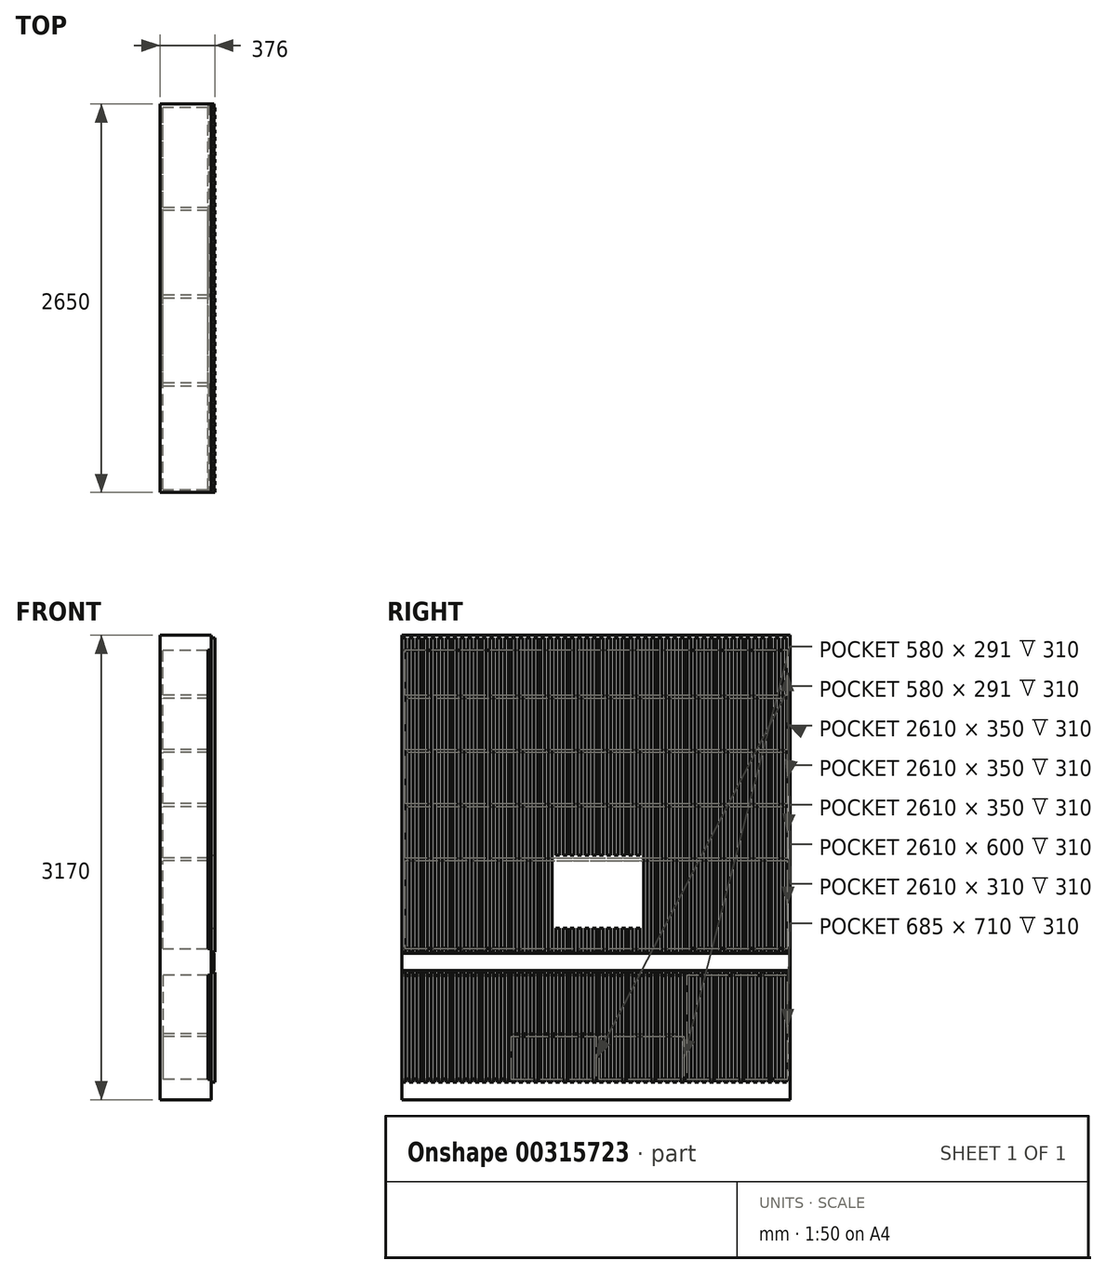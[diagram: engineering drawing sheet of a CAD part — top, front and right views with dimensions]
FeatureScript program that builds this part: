
annotation { "Feature Type Name" : "Feature", "Feature Type Description" : "" }
export const myFeature = defineFeature(function(context is Context, id is Id, definition is map)
    precondition{}
    {
        {
            var Q0;
            Q0=qCreatedBy(makeId("Top.planeOp"),FACE);
            var sketch = newSketch(context, id + "F0", { "sketchPlane" : qUnion([Q0])});
            skLineSegment(sketch, "E0.bottom", {"start": v(0, 0) * mm, "end": v(350, 0) * mm});
            skLineSegment(sketch, "E0.top", {"start": v(0, 2650) * mm, "end": v(350, 2650) * mm});
            skLineSegment(sketch, "E0.left", {"start": v(0, 0) * mm, "end": v(0, 2650) * mm});
            skLineSegment(sketch, "E0.right", {"start": v(350, 0) * mm, "end": v(350, 2650) * mm});
            skLineSegment(sketch, "E1", {"start": v(0, 2770) * mm, "end": v(350, 2770) * mm, "construction": true});
            skSolve(sketch);
        }
        {
            var Q0;
            Q0=qCreatedBy(makeId("Top.planeOp"),FACE);
            cPlane(context, id + "F1", {"entities" : qUnion([Q0]), "cplaneType" : CPlaneType.OFFSET, "offset" : 120 * mm, "width" : 150 * mm, "height" : 150 * mm});
        }
        {
            var Q0;
            Q0=makeQuery(id+"F0.imprint","IMPRINT",FACE,{"disambiguationData":[TD([[makeQuery(id+"F0.imprint","IMPRINT",EDGE,{"derivedFrom":sQuery(id+"F0.wireOp",EDGE,"E0.bottom")}),1.0]])]});
            extrude(context, id + "F2", {"entities" : qUnion([Q0]), "depth" : 3170 * mm});
        }
        {
            var Q0;
            Q0=makeQuery(id+"F2.opExtrude","SWEPT_FACE",FACE,{"disambiguationData":[OSD([sQuery(id+"F0.wireOp",EDGE,"E0.right")])]});
            var sketch = newSketch(context, id + "F3", { "sketchPlane" : qUnion([Q0])});
            skLineSegment(sketch, "E2.bottom", {"start": v(1035, 1670) * mm, "end": v(1635, 1670) * mm});
            skLineSegment(sketch, "E2.top", {"start": v(1035, 1170) * mm, "end": v(1635, 1170) * mm});
            skLineSegment(sketch, "E2.left", {"start": v(1035, 1670) * mm, "end": v(1035, 1170) * mm});
            skLineSegment(sketch, "E2.right", {"start": v(1635, 1670) * mm, "end": v(1635, 1170) * mm});
            skLineSegment(sketch, "E3", {"start": v(1035, 1670) * mm, "end": v(1635, 1170) * mm, "construction": true});
            skLineSegment(sketch, "E4", {"start": v(1635, 1670) * mm, "end": v(1035, 1170) * mm, "construction": true});
            skLineSegment(sketch, "E5", {"start": v(1335, 1420) * mm, "end": v(866.73, 1420) * mm, "construction": true});
            skPoint(sketch, "E5.endSnap0", {"position": v(1035, 1420) * mm});
            skLineSegment(sketch, "E6.bottom", {"start": v(1885, 1770) * mm, "end": v(785, 1770) * mm, "construction": true});
            skLineSegment(sketch, "E6.top", {"start": v(1885, 1070) * mm, "end": v(785, 1070) * mm, "construction": true});
            skLineSegment(sketch, "E6.left", {"start": v(1885, 1770) * mm, "end": v(1885, 1070) * mm, "construction": true});
            skLineSegment(sketch, "E6.right", {"start": v(785, 1770) * mm, "end": v(785, 1070) * mm, "construction": true});
            skPoint(sketch, "E6.middle", {"position": v(1335, 1420) * mm});
            skSolve(sketch);
        }
        {
            var Q0;
            Q0=qCreatedBy(makeId("Top.planeOp"),FACE);
            cPlane(context, id + "F4", {"entities" : qUnion([Q0]), "cplaneType" : CPlaneType.OFFSET, "offset" : 3150 * mm, "width" : 150 * mm, "height" : 150 * mm});
        }
        {
            var Q0;
            Q0=qCreatedBy(id+"F1.planeOp",FACE);
            var sketch = newSketch(context, id + "F5", { "sketchPlane" : qUnion([Q0])});
            skLineSegment(sketch, "E7.bottom", {"start": v(351, 0) * mm, "end": v(376, 0) * mm});
            skLineSegment(sketch, "E7.top", {"start": v(351, 25) * mm, "end": v(376, 25) * mm});
            skLineSegment(sketch, "E7.left", {"start": v(351, 0) * mm, "end": v(351, 25) * mm});
            skLineSegment(sketch, "E7.right", {"start": v(376, 0) * mm, "end": v(376, 25) * mm});
            skLineSegment(sketch, "E8.0.1.0", {"start": v(351, 75) * mm, "end": v(376, 75) * mm});
            skLineSegment(sketch, "E8.0.1.1", {"start": v(351, 50) * mm, "end": v(376, 50) * mm});
            skLineSegment(sketch, "E8.0.1.2", {"start": v(376, 50) * mm, "end": v(376, 75) * mm});
            skLineSegment(sketch, "E8.0.1.3", {"start": v(351, 50) * mm, "end": v(351, 75) * mm});
            skLineSegment(sketch, "E8.0.2.0", {"start": v(351, 125) * mm, "end": v(376, 125) * mm});
            skLineSegment(sketch, "E8.0.2.1", {"start": v(351, 100) * mm, "end": v(376, 100) * mm});
            skLineSegment(sketch, "E8.0.2.2", {"start": v(376, 100) * mm, "end": v(376, 125) * mm});
            skLineSegment(sketch, "E8.0.2.3", {"start": v(351, 100) * mm, "end": v(351, 125) * mm});
            skLineSegment(sketch, "E8.0.3.0", {"start": v(351, 175) * mm, "end": v(376, 175) * mm});
            skLineSegment(sketch, "E8.0.3.1", {"start": v(351, 150) * mm, "end": v(376, 150) * mm});
            skLineSegment(sketch, "E8.0.3.2", {"start": v(376, 150) * mm, "end": v(376, 175) * mm});
            skLineSegment(sketch, "E8.0.3.3", {"start": v(351, 150) * mm, "end": v(351, 175) * mm});
            skLineSegment(sketch, "E8.0.4.0", {"start": v(351, 225) * mm, "end": v(376, 225) * mm});
            skLineSegment(sketch, "E8.0.4.1", {"start": v(351, 200) * mm, "end": v(376, 200) * mm});
            skLineSegment(sketch, "E8.0.4.2", {"start": v(376, 200) * mm, "end": v(376, 225) * mm});
            skLineSegment(sketch, "E8.0.4.3", {"start": v(351, 200) * mm, "end": v(351, 225) * mm});
            skLineSegment(sketch, "E8.0.5.0", {"start": v(351, 275) * mm, "end": v(376, 275) * mm});
            skLineSegment(sketch, "E8.0.5.1", {"start": v(351, 250) * mm, "end": v(376, 250) * mm});
            skLineSegment(sketch, "E8.0.5.2", {"start": v(376, 250) * mm, "end": v(376, 275) * mm});
            skLineSegment(sketch, "E8.0.5.3", {"start": v(351, 250) * mm, "end": v(351, 275) * mm});
            skLineSegment(sketch, "E8.0.6.0", {"start": v(351, 325) * mm, "end": v(376, 325) * mm});
            skLineSegment(sketch, "E8.0.6.1", {"start": v(351, 300) * mm, "end": v(376, 300) * mm});
            skLineSegment(sketch, "E8.0.6.2", {"start": v(376, 300) * mm, "end": v(376, 325) * mm});
            skLineSegment(sketch, "E8.0.6.3", {"start": v(351, 300) * mm, "end": v(351, 325) * mm});
            skLineSegment(sketch, "E8.0.7.0", {"start": v(351, 375) * mm, "end": v(376, 375) * mm});
            skLineSegment(sketch, "E8.0.7.1", {"start": v(351, 350) * mm, "end": v(376, 350) * mm});
            skLineSegment(sketch, "E8.0.7.2", {"start": v(376, 350) * mm, "end": v(376, 375) * mm});
            skLineSegment(sketch, "E8.0.7.3", {"start": v(351, 350) * mm, "end": v(351, 375) * mm});
            skLineSegment(sketch, "E8.0.8.0", {"start": v(351, 425) * mm, "end": v(376, 425) * mm});
            skLineSegment(sketch, "E8.0.8.1", {"start": v(351, 400) * mm, "end": v(376, 400) * mm});
            skLineSegment(sketch, "E8.0.8.2", {"start": v(376, 400) * mm, "end": v(376, 425) * mm});
            skLineSegment(sketch, "E8.0.8.3", {"start": v(351, 400) * mm, "end": v(351, 425) * mm});
            skLineSegment(sketch, "E8.0.9.0", {"start": v(351, 475) * mm, "end": v(376, 475) * mm});
            skLineSegment(sketch, "E8.0.9.1", {"start": v(351, 450) * mm, "end": v(376, 450) * mm});
            skLineSegment(sketch, "E8.0.9.2", {"start": v(376, 450) * mm, "end": v(376, 475) * mm});
            skLineSegment(sketch, "E8.0.9.3", {"start": v(351, 450) * mm, "end": v(351, 475) * mm});
            skLineSegment(sketch, "E8.0.10.0", {"start": v(351, 525) * mm, "end": v(376, 525) * mm});
            skLineSegment(sketch, "E8.0.10.1", {"start": v(351, 500) * mm, "end": v(376, 500) * mm});
            skLineSegment(sketch, "E8.0.10.2", {"start": v(376, 500) * mm, "end": v(376, 525) * mm});
            skLineSegment(sketch, "E8.0.10.3", {"start": v(351, 500) * mm, "end": v(351, 525) * mm});
            skLineSegment(sketch, "E8.0.11.0", {"start": v(351, 575) * mm, "end": v(376, 575) * mm});
            skLineSegment(sketch, "E8.0.11.1", {"start": v(351, 550) * mm, "end": v(376, 550) * mm});
            skLineSegment(sketch, "E8.0.11.2", {"start": v(376, 550) * mm, "end": v(376, 575) * mm});
            skLineSegment(sketch, "E8.0.11.3", {"start": v(351, 550) * mm, "end": v(351, 575) * mm});
            skLineSegment(sketch, "E8.0.12.0", {"start": v(351, 625) * mm, "end": v(376, 625) * mm});
            skLineSegment(sketch, "E8.0.12.1", {"start": v(351, 600) * mm, "end": v(376, 600) * mm});
            skLineSegment(sketch, "E8.0.12.2", {"start": v(376, 600) * mm, "end": v(376, 625) * mm});
            skLineSegment(sketch, "E8.0.12.3", {"start": v(351, 600) * mm, "end": v(351, 625) * mm});
            skLineSegment(sketch, "E8.0.13.0", {"start": v(351, 675) * mm, "end": v(376, 675) * mm});
            skLineSegment(sketch, "E8.0.13.1", {"start": v(351, 650) * mm, "end": v(376, 650) * mm});
            skLineSegment(sketch, "E8.0.13.2", {"start": v(376, 650) * mm, "end": v(376, 675) * mm});
            skLineSegment(sketch, "E8.0.13.3", {"start": v(351, 650) * mm, "end": v(351, 675) * mm});
            skLineSegment(sketch, "E8.0.14.0", {"start": v(351, 725) * mm, "end": v(376, 725) * mm});
            skLineSegment(sketch, "E8.0.14.1", {"start": v(351, 700) * mm, "end": v(376, 700) * mm});
            skLineSegment(sketch, "E8.0.14.2", {"start": v(376, 700) * mm, "end": v(376, 725) * mm});
            skLineSegment(sketch, "E8.0.14.3", {"start": v(351, 700) * mm, "end": v(351, 725) * mm});
            skLineSegment(sketch, "E8.0.15.0", {"start": v(351, 775) * mm, "end": v(376, 775) * mm});
            skLineSegment(sketch, "E8.0.15.1", {"start": v(351, 750) * mm, "end": v(376, 750) * mm});
            skLineSegment(sketch, "E8.0.15.2", {"start": v(376, 750) * mm, "end": v(376, 775) * mm});
            skLineSegment(sketch, "E8.0.15.3", {"start": v(351, 750) * mm, "end": v(351, 775) * mm});
            skLineSegment(sketch, "E8.0.16.0", {"start": v(351, 825) * mm, "end": v(376, 825) * mm});
            skLineSegment(sketch, "E8.0.16.1", {"start": v(351, 800) * mm, "end": v(376, 800) * mm});
            skLineSegment(sketch, "E8.0.16.2", {"start": v(376, 800) * mm, "end": v(376, 825) * mm});
            skLineSegment(sketch, "E8.0.16.3", {"start": v(351, 800) * mm, "end": v(351, 825) * mm});
            skLineSegment(sketch, "E8.0.17.0", {"start": v(351, 875) * mm, "end": v(376, 875) * mm});
            skLineSegment(sketch, "E8.0.17.1", {"start": v(351, 850) * mm, "end": v(376, 850) * mm});
            skLineSegment(sketch, "E8.0.17.2", {"start": v(376, 850) * mm, "end": v(376, 875) * mm});
            skLineSegment(sketch, "E8.0.17.3", {"start": v(351, 850) * mm, "end": v(351, 875) * mm});
            skLineSegment(sketch, "E8.0.18.0", {"start": v(351, 925) * mm, "end": v(376, 925) * mm});
            skLineSegment(sketch, "E8.0.18.1", {"start": v(351, 900) * mm, "end": v(376, 900) * mm});
            skLineSegment(sketch, "E8.0.18.2", {"start": v(376, 900) * mm, "end": v(376, 925) * mm});
            skLineSegment(sketch, "E8.0.18.3", {"start": v(351, 900) * mm, "end": v(351, 925) * mm});
            skLineSegment(sketch, "E8.0.19.0", {"start": v(351, 975) * mm, "end": v(376, 975) * mm});
            skLineSegment(sketch, "E8.0.19.1", {"start": v(351, 950) * mm, "end": v(376, 950) * mm});
            skLineSegment(sketch, "E8.0.19.2", {"start": v(376, 950) * mm, "end": v(376, 975) * mm});
            skLineSegment(sketch, "E8.0.19.3", {"start": v(351, 950) * mm, "end": v(351, 975) * mm});
            skLineSegment(sketch, "E8.0.20.0", {"start": v(351, 1025) * mm, "end": v(376, 1025) * mm});
            skLineSegment(sketch, "E8.0.20.1", {"start": v(351, 1000) * mm, "end": v(376, 1000) * mm});
            skLineSegment(sketch, "E8.0.20.2", {"start": v(376, 1000) * mm, "end": v(376, 1025) * mm});
            skLineSegment(sketch, "E8.0.20.3", {"start": v(351, 1000) * mm, "end": v(351, 1025) * mm});
            skLineSegment(sketch, "E8.0.21.0", {"start": v(351, 1075) * mm, "end": v(376, 1075) * mm});
            skLineSegment(sketch, "E8.0.21.1", {"start": v(351, 1050) * mm, "end": v(376, 1050) * mm});
            skLineSegment(sketch, "E8.0.21.2", {"start": v(376, 1050) * mm, "end": v(376, 1075) * mm});
            skLineSegment(sketch, "E8.0.21.3", {"start": v(351, 1050) * mm, "end": v(351, 1075) * mm});
            skLineSegment(sketch, "E8.direction1", {"start": v(351, 0) * mm, "end": v(376, 0) * mm, "construction": true});
            skLineSegment(sketch, "E8.direction2", {"start": v(351, 0) * mm, "end": v(351, 50) * mm, "construction": true});
            skLineSegment(sketch, "E9.0.0.22", {"start": v(351, 1125) * mm, "end": v(376, 1125) * mm});
            skLineSegment(sketch, "E9.3.0.22", {"start": v(351, 1100) * mm, "end": v(376, 1100) * mm});
            skLineSegment(sketch, "E9.6.0.22", {"start": v(376, 1100) * mm, "end": v(376, 1125) * mm});
            skLineSegment(sketch, "E9.9.0.22", {"start": v(351, 1100) * mm, "end": v(351, 1125) * mm});
            skLineSegment(sketch, "E9.0.0.23", {"start": v(351, 1175) * mm, "end": v(376, 1175) * mm});
            skLineSegment(sketch, "E9.3.0.23", {"start": v(351, 1150) * mm, "end": v(376, 1150) * mm});
            skLineSegment(sketch, "E9.6.0.23", {"start": v(376, 1150) * mm, "end": v(376, 1175) * mm});
            skLineSegment(sketch, "E9.9.0.23", {"start": v(351, 1150) * mm, "end": v(351, 1175) * mm});
            skLineSegment(sketch, "E9.0.0.24", {"start": v(351, 1225) * mm, "end": v(376, 1225) * mm});
            skLineSegment(sketch, "E9.3.0.24", {"start": v(351, 1200) * mm, "end": v(376, 1200) * mm});
            skLineSegment(sketch, "E9.6.0.24", {"start": v(376, 1200) * mm, "end": v(376, 1225) * mm});
            skLineSegment(sketch, "E9.9.0.24", {"start": v(351, 1200) * mm, "end": v(351, 1225) * mm});
            skLineSegment(sketch, "E10.0.0.25", {"start": v(351, 1275) * mm, "end": v(376, 1275) * mm});
            skLineSegment(sketch, "E10.3.0.25", {"start": v(351, 1250) * mm, "end": v(376, 1250) * mm});
            skLineSegment(sketch, "E10.6.0.25", {"start": v(376, 1250) * mm, "end": v(376, 1275) * mm});
            skLineSegment(sketch, "E10.9.0.25", {"start": v(351, 1250) * mm, "end": v(351, 1275) * mm});
            skLineSegment(sketch, "E10.0.0.26", {"start": v(351, 1325) * mm, "end": v(376, 1325) * mm});
            skLineSegment(sketch, "E10.3.0.26", {"start": v(351, 1300) * mm, "end": v(376, 1300) * mm});
            skLineSegment(sketch, "E10.6.0.26", {"start": v(376, 1300) * mm, "end": v(376, 1325) * mm});
            skLineSegment(sketch, "E10.9.0.26", {"start": v(351, 1300) * mm, "end": v(351, 1325) * mm});
            skLineSegment(sketch, "E10.0.0.27", {"start": v(351, 1375) * mm, "end": v(376, 1375) * mm});
            skLineSegment(sketch, "E10.3.0.27", {"start": v(351, 1350) * mm, "end": v(376, 1350) * mm});
            skLineSegment(sketch, "E10.6.0.27", {"start": v(376, 1350) * mm, "end": v(376, 1375) * mm});
            skLineSegment(sketch, "E10.9.0.27", {"start": v(351, 1350) * mm, "end": v(351, 1375) * mm});
            skLineSegment(sketch, "E10.0.0.28", {"start": v(351, 1425) * mm, "end": v(376, 1425) * mm});
            skLineSegment(sketch, "E10.3.0.28", {"start": v(351, 1400) * mm, "end": v(376, 1400) * mm});
            skLineSegment(sketch, "E10.6.0.28", {"start": v(376, 1400) * mm, "end": v(376, 1425) * mm});
            skLineSegment(sketch, "E10.9.0.28", {"start": v(351, 1400) * mm, "end": v(351, 1425) * mm});
            skLineSegment(sketch, "E10.0.0.29", {"start": v(351, 1475) * mm, "end": v(376, 1475) * mm});
            skLineSegment(sketch, "E10.3.0.29", {"start": v(351, 1450) * mm, "end": v(376, 1450) * mm});
            skLineSegment(sketch, "E10.6.0.29", {"start": v(376, 1450) * mm, "end": v(376, 1475) * mm});
            skLineSegment(sketch, "E10.9.0.29", {"start": v(351, 1450) * mm, "end": v(351, 1475) * mm});
            skLineSegment(sketch, "E10.0.0.30", {"start": v(351, 1525) * mm, "end": v(376, 1525) * mm});
            skLineSegment(sketch, "E10.3.0.30", {"start": v(351, 1500) * mm, "end": v(376, 1500) * mm});
            skLineSegment(sketch, "E10.6.0.30", {"start": v(376, 1500) * mm, "end": v(376, 1525) * mm});
            skLineSegment(sketch, "E10.9.0.30", {"start": v(351, 1500) * mm, "end": v(351, 1525) * mm});
            skLineSegment(sketch, "E10.0.0.31", {"start": v(351, 1575) * mm, "end": v(376, 1575) * mm});
            skLineSegment(sketch, "E10.3.0.31", {"start": v(351, 1550) * mm, "end": v(376, 1550) * mm});
            skLineSegment(sketch, "E10.6.0.31", {"start": v(376, 1550) * mm, "end": v(376, 1575) * mm});
            skLineSegment(sketch, "E10.9.0.31", {"start": v(351, 1550) * mm, "end": v(351, 1575) * mm});
            skLineSegment(sketch, "E10.0.0.32", {"start": v(351, 1625) * mm, "end": v(376, 1625) * mm});
            skLineSegment(sketch, "E10.3.0.32", {"start": v(351, 1600) * mm, "end": v(376, 1600) * mm});
            skLineSegment(sketch, "E10.6.0.32", {"start": v(376, 1600) * mm, "end": v(376, 1625) * mm});
            skLineSegment(sketch, "E10.9.0.32", {"start": v(351, 1600) * mm, "end": v(351, 1625) * mm});
            skLineSegment(sketch, "E10.0.0.33", {"start": v(351, 1675) * mm, "end": v(376, 1675) * mm});
            skLineSegment(sketch, "E10.3.0.33", {"start": v(351, 1650) * mm, "end": v(376, 1650) * mm});
            skLineSegment(sketch, "E10.6.0.33", {"start": v(376, 1650) * mm, "end": v(376, 1675) * mm});
            skLineSegment(sketch, "E10.9.0.33", {"start": v(351, 1650) * mm, "end": v(351, 1675) * mm});
            skLineSegment(sketch, "E10.0.0.34", {"start": v(351, 1725) * mm, "end": v(376, 1725) * mm});
            skLineSegment(sketch, "E10.3.0.34", {"start": v(351, 1700) * mm, "end": v(376, 1700) * mm});
            skLineSegment(sketch, "E10.6.0.34", {"start": v(376, 1700) * mm, "end": v(376, 1725) * mm});
            skLineSegment(sketch, "E10.9.0.34", {"start": v(351, 1700) * mm, "end": v(351, 1725) * mm});
            skLineSegment(sketch, "E10.0.0.35", {"start": v(351, 1775) * mm, "end": v(376, 1775) * mm});
            skLineSegment(sketch, "E10.3.0.35", {"start": v(351, 1750) * mm, "end": v(376, 1750) * mm});
            skLineSegment(sketch, "E10.6.0.35", {"start": v(376, 1750) * mm, "end": v(376, 1775) * mm});
            skLineSegment(sketch, "E10.9.0.35", {"start": v(351, 1750) * mm, "end": v(351, 1775) * mm});
            skLineSegment(sketch, "E10.0.0.36", {"start": v(351, 1825) * mm, "end": v(376, 1825) * mm});
            skLineSegment(sketch, "E10.3.0.36", {"start": v(351, 1800) * mm, "end": v(376, 1800) * mm});
            skLineSegment(sketch, "E10.6.0.36", {"start": v(376, 1800) * mm, "end": v(376, 1825) * mm});
            skLineSegment(sketch, "E10.9.0.36", {"start": v(351, 1800) * mm, "end": v(351, 1825) * mm});
            skLineSegment(sketch, "E10.0.0.37", {"start": v(351, 1875) * mm, "end": v(376, 1875) * mm});
            skLineSegment(sketch, "E10.3.0.37", {"start": v(351, 1850) * mm, "end": v(376, 1850) * mm});
            skLineSegment(sketch, "E10.6.0.37", {"start": v(376, 1850) * mm, "end": v(376, 1875) * mm});
            skLineSegment(sketch, "E10.9.0.37", {"start": v(351, 1850) * mm, "end": v(351, 1875) * mm});
            skLineSegment(sketch, "E10.0.0.38", {"start": v(351, 1925) * mm, "end": v(376, 1925) * mm});
            skLineSegment(sketch, "E10.3.0.38", {"start": v(351, 1900) * mm, "end": v(376, 1900) * mm});
            skLineSegment(sketch, "E10.6.0.38", {"start": v(376, 1900) * mm, "end": v(376, 1925) * mm});
            skLineSegment(sketch, "E10.9.0.38", {"start": v(351, 1900) * mm, "end": v(351, 1925) * mm});
            skLineSegment(sketch, "E10.0.0.39", {"start": v(351, 1975) * mm, "end": v(376, 1975) * mm});
            skLineSegment(sketch, "E10.3.0.39", {"start": v(351, 1950) * mm, "end": v(376, 1950) * mm});
            skLineSegment(sketch, "E10.6.0.39", {"start": v(376, 1950) * mm, "end": v(376, 1975) * mm});
            skLineSegment(sketch, "E10.9.0.39", {"start": v(351, 1950) * mm, "end": v(351, 1975) * mm});
            skLineSegment(sketch, "E10.0.0.40", {"start": v(351, 2025) * mm, "end": v(376, 2025) * mm});
            skLineSegment(sketch, "E10.3.0.40", {"start": v(351, 2000) * mm, "end": v(376, 2000) * mm});
            skLineSegment(sketch, "E10.6.0.40", {"start": v(376, 2000) * mm, "end": v(376, 2025) * mm});
            skLineSegment(sketch, "E10.9.0.40", {"start": v(351, 2000) * mm, "end": v(351, 2025) * mm});
            skLineSegment(sketch, "E10.0.0.41", {"start": v(351, 2075) * mm, "end": v(376, 2075) * mm});
            skLineSegment(sketch, "E10.3.0.41", {"start": v(351, 2050) * mm, "end": v(376, 2050) * mm});
            skLineSegment(sketch, "E10.6.0.41", {"start": v(376, 2050) * mm, "end": v(376, 2075) * mm});
            skLineSegment(sketch, "E10.9.0.41", {"start": v(351, 2050) * mm, "end": v(351, 2075) * mm});
            skLineSegment(sketch, "E10.0.0.42", {"start": v(351, 2125) * mm, "end": v(376, 2125) * mm});
            skLineSegment(sketch, "E10.3.0.42", {"start": v(351, 2100) * mm, "end": v(376, 2100) * mm});
            skLineSegment(sketch, "E10.6.0.42", {"start": v(376, 2100) * mm, "end": v(376, 2125) * mm});
            skLineSegment(sketch, "E10.9.0.42", {"start": v(351, 2100) * mm, "end": v(351, 2125) * mm});
            skLineSegment(sketch, "E10.0.0.43", {"start": v(351, 2175) * mm, "end": v(376, 2175) * mm});
            skLineSegment(sketch, "E10.3.0.43", {"start": v(351, 2150) * mm, "end": v(376, 2150) * mm});
            skLineSegment(sketch, "E10.6.0.43", {"start": v(376, 2150) * mm, "end": v(376, 2175) * mm});
            skLineSegment(sketch, "E10.9.0.43", {"start": v(351, 2150) * mm, "end": v(351, 2175) * mm});
            skLineSegment(sketch, "E10.0.0.44", {"start": v(351, 2225) * mm, "end": v(376, 2225) * mm});
            skLineSegment(sketch, "E10.3.0.44", {"start": v(351, 2200) * mm, "end": v(376, 2200) * mm});
            skLineSegment(sketch, "E10.6.0.44", {"start": v(376, 2200) * mm, "end": v(376, 2225) * mm});
            skLineSegment(sketch, "E10.9.0.44", {"start": v(351, 2200) * mm, "end": v(351, 2225) * mm});
            skLineSegment(sketch, "E10.0.0.45", {"start": v(351, 2275) * mm, "end": v(376, 2275) * mm});
            skLineSegment(sketch, "E10.3.0.45", {"start": v(351, 2250) * mm, "end": v(376, 2250) * mm});
            skLineSegment(sketch, "E10.6.0.45", {"start": v(376, 2250) * mm, "end": v(376, 2275) * mm});
            skLineSegment(sketch, "E10.9.0.45", {"start": v(351, 2250) * mm, "end": v(351, 2275) * mm});
            skLineSegment(sketch, "E10.0.0.46", {"start": v(351, 2325) * mm, "end": v(376, 2325) * mm});
            skLineSegment(sketch, "E10.3.0.46", {"start": v(351, 2300) * mm, "end": v(376, 2300) * mm});
            skLineSegment(sketch, "E10.6.0.46", {"start": v(376, 2300) * mm, "end": v(376, 2325) * mm});
            skLineSegment(sketch, "E10.9.0.46", {"start": v(351, 2300) * mm, "end": v(351, 2325) * mm});
            skLineSegment(sketch, "E10.0.0.47", {"start": v(351, 2375) * mm, "end": v(376, 2375) * mm});
            skLineSegment(sketch, "E10.3.0.47", {"start": v(351, 2350) * mm, "end": v(376, 2350) * mm});
            skLineSegment(sketch, "E10.6.0.47", {"start": v(376, 2350) * mm, "end": v(376, 2375) * mm});
            skLineSegment(sketch, "E10.9.0.47", {"start": v(351, 2350) * mm, "end": v(351, 2375) * mm});
            skLineSegment(sketch, "E10.0.0.48", {"start": v(351, 2425) * mm, "end": v(376, 2425) * mm});
            skLineSegment(sketch, "E10.3.0.48", {"start": v(351, 2400) * mm, "end": v(376, 2400) * mm});
            skLineSegment(sketch, "E10.6.0.48", {"start": v(376, 2400) * mm, "end": v(376, 2425) * mm});
            skLineSegment(sketch, "E10.9.0.48", {"start": v(351, 2400) * mm, "end": v(351, 2425) * mm});
            skLineSegment(sketch, "E10.0.0.49", {"start": v(351, 2475) * mm, "end": v(376, 2475) * mm});
            skLineSegment(sketch, "E10.3.0.49", {"start": v(351, 2450) * mm, "end": v(376, 2450) * mm});
            skLineSegment(sketch, "E10.6.0.49", {"start": v(376, 2450) * mm, "end": v(376, 2475) * mm});
            skLineSegment(sketch, "E10.9.0.49", {"start": v(351, 2450) * mm, "end": v(351, 2475) * mm});
            skLineSegment(sketch, "E11.0.0.50", {"start": v(351, 2525) * mm, "end": v(376, 2525) * mm});
            skLineSegment(sketch, "E11.3.0.50", {"start": v(351, 2500) * mm, "end": v(376, 2500) * mm});
            skLineSegment(sketch, "E11.6.0.50", {"start": v(376, 2500) * mm, "end": v(376, 2525) * mm});
            skLineSegment(sketch, "E11.9.0.50", {"start": v(351, 2500) * mm, "end": v(351, 2525) * mm});
            skLineSegment(sketch, "E11.0.0.51", {"start": v(351, 2575) * mm, "end": v(376, 2575) * mm});
            skLineSegment(sketch, "E11.3.0.51", {"start": v(351, 2550) * mm, "end": v(376, 2550) * mm});
            skLineSegment(sketch, "E11.6.0.51", {"start": v(376, 2550) * mm, "end": v(376, 2575) * mm});
            skLineSegment(sketch, "E11.9.0.51", {"start": v(351, 2550) * mm, "end": v(351, 2575) * mm});
            skLineSegment(sketch, "E11.0.0.52", {"start": v(351, 2625) * mm, "end": v(376, 2625) * mm});
            skLineSegment(sketch, "E11.3.0.52", {"start": v(351, 2600) * mm, "end": v(376, 2600) * mm});
            skLineSegment(sketch, "E11.6.0.52", {"start": v(376, 2600) * mm, "end": v(376, 2625) * mm});
            skLineSegment(sketch, "E11.9.0.52", {"start": v(351, 2600) * mm, "end": v(351, 2625) * mm});
            skSolve(sketch);
        }
        {
            var Q0;
            Q0=qSketchRegion(id+"F5",true);
            var Q1;
            Q1=qCreatedBy(id+"F4.planeOp",FACE);
            extrude(context, id + "F6", {"entities" : qUnion([Q0]), "endBound" : BoundingType.UP_TO_SURFACE, "endBoundEntityFace" : qUnion([Q1]), "depth" : 2525 * mm});
        }
        {
            var Q0;
            Q0 = qSketchRegion(id + "F3", true);
            extrude(context, id + "F7", {"entities" : qUnion([Q0]), "operationType" : NewBodyOperationType.REMOVE, "endBound" : BoundingType.THROUGH_ALL, "depth" : 25 * mm});
        }
        {
            var Q0;
            Q0=makeQuery(id+"F2.opExtrude","SWEPT_FACE",FACE,{"disambiguationData":[OSD([sQuery(id+"F0.wireOp",EDGE,"E0.left")])]});
            cPlane(context, id + "F8", {"entities" : qUnion([Q0]), "cplaneType" : CPlaneType.OFFSET, "offset" : 20 * mm, "oppositeDirection" : true, "width" : 150 * mm, "height" : 150 * mm});
        }
        {
            var Q0;
            Q0=makeQuery(id+"F2.opExtrude","SWEPT_FACE",FACE,{"disambiguationData":[OSD([sQuery(id+"F0.wireOp",EDGE,"E0.right")])]});
            var sketch = newSketch(context, id + "F9", { "sketchPlane" : qUnion([Q0])});
            skLineSegment(sketch, "E12.bottom", {"start": v(-252.85, 1010) * mm, "end": v(2905.96, 1010) * mm});
            skLineSegment(sketch, "E12.top", {"start": v(-252.85, 870) * mm, "end": v(2905.96, 870) * mm});
            skLineSegment(sketch, "E12.left", {"start": v(-252.85, 1010) * mm, "end": v(-252.85, 870) * mm});
            skLineSegment(sketch, "E12.right", {"start": v(2905.96, 1010) * mm, "end": v(2905.96, 870) * mm});
            skSolve(sketch);
        }
        {
            var Q0;
            Q0 = qSketchRegion(id + "F9", true);
            extrude(context, id + "F10", {"entities" : qUnion([Q0]), "operationType" : NewBodyOperationType.REMOVE, "endBound" : BoundingType.THROUGH_ALL, "depth" : 25 * mm});
        }
        {
            var Q0;
            {var subQ1=sQuery(id+"F0.wireOp",EDGE,"E0.right");var subQ6=makeQuery(id+"F2.opExtrude","CAP_EDGE",EDGE,{"disambiguationData":[OSD([subQ1])],"isStart":true});Q0=makeQuery(id+"F9.imprint","IMPRINT",FACE,{"disambiguationData":[TD([[makeQuery(id+"F9.imprint","IMPRINT",EDGE,{"derivedFrom":subQ6}),1.0]])]});}
            cPlane(context, id + "F11", {"entities" : qUnion([Q0]), "cplaneType" : CPlaneType.OFFSET, "offset" : 20 * mm, "oppositeDirection" : true, "width" : 150 * mm, "height" : 150 * mm});
        }
        {
            var Q0;
            Q0=makeQuery(id+"F3.imprint","IMPRINT",FACE,{"disambiguationData":[TD([[makeQuery(id+"F3.imprint","IMPRINT",EDGE,{"derivedFrom":sQuery(id+"F3.wireOp",EDGE,"E2.bottom")}),1.0]])]});
            var sketch = newSketch(context, id + "F12", { "sketchPlane" : qUnion([Q0])});
            skLineSegment(sketch, "E13.bottom", {"start": v(0, 1000) * mm, "end": v(2650, 1000) * mm});
            skLineSegment(sketch, "E13.top", {"start": v(0, 880) * mm, "end": v(2650, 880) * mm});
            skLineSegment(sketch, "E13.left", {"start": v(0, 1000) * mm, "end": v(0, 880) * mm});
            skLineSegment(sketch, "E13.right", {"start": v(2650, 1000) * mm, "end": v(2650, 880) * mm});
            skSolve(sketch);
        }
        {
            var Q0;
            Q0 = qSketchRegion(id + "F12", true);
            extrude(context, id + "F13", {"entities" : qUnion([Q0]), "depth" : 20 * mm});
        }
        {
            var Q0;
            Q0=makeQuery(id+"F3.imprint","IMPRINT",FACE,{"disambiguationData":[TD([[makeQuery(id+"F3.imprint","IMPRINT",EDGE,{"derivedFrom":sQuery(id+"F3.wireOp",EDGE,"E2.bottom")}),1.0]])]});
            var sketch = newSketch(context, id + "F14", { "sketchPlane" : qUnion([Q0])});
            skLineSegment(sketch, "E14.bottom", {"start": v(0, 850) * mm, "end": v(2650, 850) * mm});
            skLineSegment(sketch, "E14.top", {"start": v(0, 140) * mm, "end": v(2650, 140) * mm});
            skLineSegment(sketch, "E14.left", {"start": v(0, 850) * mm, "end": v(0, 140) * mm});
            skLineSegment(sketch, "E14.right", {"start": v(2650, 850) * mm, "end": v(2650, 140) * mm});
            skLineSegment(sketch, "E15.bottom", {"start": v(0, 3070) * mm, "end": v(2650, 3070) * mm});
            skLineSegment(sketch, "E15.top", {"start": v(0, 1030) * mm, "end": v(2650, 1030) * mm});
            skLineSegment(sketch, "E15.left", {"start": v(0, 3070) * mm, "end": v(0, 1030) * mm});
            skLineSegment(sketch, "E15.right", {"start": v(2650, 3070) * mm, "end": v(2650, 1030) * mm});
            skSolve(sketch);
        }
        {
            var Q0;
            Q0 = qSketchRegion(id + "F14", true);
            var Q1;
            Q1=qCreatedBy(id+"F11.planeOp",FACE);
            extrude(context, id + "F15", {"entities" : qUnion([Q0]), "operationType" : NewBodyOperationType.REMOVE, "endBound" : BoundingType.UP_TO_SURFACE, "oppositeDirection" : true, "endBoundEntityFace" : qUnion([Q1]), "depth" : 20 * mm});
        }
        {
            var Q0;
            Q0=qCreatedBy(id+"F11.planeOp",FACE);
            var sketch = newSketch(context, id + "F16", { "sketchPlane" : qUnion([Q0])});
            skLineSegment(sketch, "E16.bottom", {"start": v(20, 850) * mm, "end": v(2630, 850) * mm});
            skLineSegment(sketch, "E16.top", {"start": v(20, 140) * mm, "end": v(2630, 140) * mm});
            skLineSegment(sketch, "E16.left", {"start": v(20, 850) * mm, "end": v(20, 140) * mm});
            skLineSegment(sketch, "E16.right", {"start": v(2630, 850) * mm, "end": v(2630, 140) * mm});
            skLineSegment(sketch, "E17.bottom", {"start": v(20, 1030) * mm, "end": v(2630, 1030) * mm});
            skLineSegment(sketch, "E17.top", {"start": v(20, 3070) * mm, "end": v(2630, 3070) * mm});
            skLineSegment(sketch, "E17.left", {"start": v(20, 1030) * mm, "end": v(20, 3070) * mm});
            skLineSegment(sketch, "E17.right", {"start": v(2630, 1030) * mm, "end": v(2630, 3070) * mm});
            skSolve(sketch);
        }
        {
            var Q0;
            Q0 = qSketchRegion(id + "F16", true);
            var Q1;
            Q1=qCreatedBy(id+"F8.planeOp",FACE);
            extrude(context, id + "F17", {"entities" : qUnion([Q0]), "operationType" : NewBodyOperationType.REMOVE, "endBound" : BoundingType.UP_TO_SURFACE, "oppositeDirection" : true, "endBoundEntityFace" : qUnion([Q1]), "depth" : 25 * mm});
        }
        {
            var Q0;
            Q0=qCreatedBy(id+"F8.planeOp",FACE);
            var sketch = newSketch(context, id + "F18", { "sketchPlane" : qUnion([Q0])});
            skLineSegment(sketch, "E18.bottom", {"start": v(-725, 3070) * mm, "end": v(-745, 3070) * mm});
            skLineSegment(sketch, "E18.left", {"start": v(-725, 3070) * mm, "end": v(-725, 1850) * mm});
            skLineSegment(sketch, "E18.right", {"start": v(-745, 3070) * mm, "end": v(-745, 1850) * mm});
            skLineSegment(sketch, "E19.bottom", {"start": v(-1925, 3070) * mm, "end": v(-1945, 3070) * mm});
            skLineSegment(sketch, "E19.left", {"start": v(-1925, 3070) * mm, "end": v(-1925, 1850) * mm});
            skLineSegment(sketch, "E19.right", {"start": v(-1945, 3070) * mm, "end": v(-1945, 1850) * mm});
            skLineSegment(sketch, "E20.bottom", {"start": v(-1945, 850) * mm, "end": v(-1925, 850) * mm});
            skLineSegment(sketch, "E20.top", {"start": v(-1945, 140) * mm, "end": v(-1925, 140) * mm});
            skLineSegment(sketch, "E20.left", {"start": v(-1945, 850) * mm, "end": v(-1945, 140) * mm});
            skLineSegment(sketch, "E20.right", {"start": v(-1925, 850) * mm, "end": v(-1925, 140) * mm});
            skLineSegment(sketch, "E21.bottom", {"start": v(-745, 850) * mm, "end": v(-725, 850) * mm});
            skLineSegment(sketch, "E21.top", {"start": v(-745, 140) * mm, "end": v(-725, 140) * mm});
            skLineSegment(sketch, "E21.left", {"start": v(-745, 850) * mm, "end": v(-745, 140) * mm});
            skLineSegment(sketch, "E21.right", {"start": v(-725, 850) * mm, "end": v(-725, 140) * mm});
            skLineSegment(sketch, "E22.bottom", {"start": v(-1325, 850) * mm, "end": v(-1345, 850) * mm});
            skLineSegment(sketch, "E22.top", {"start": v(-1325, 140) * mm, "end": v(-1345, 140) * mm});
            skLineSegment(sketch, "E22.left", {"start": v(-1325, 850) * mm, "end": v(-1325, 140) * mm});
            skLineSegment(sketch, "E22.right", {"start": v(-1345, 850) * mm, "end": v(-1345, 140) * mm});
            skLineSegment(sketch, "E23.bottom", {"start": v(-20, 1850) * mm, "end": v(-2630, 1850) * mm});
            skLineSegment(sketch, "E23.top", {"start": v(-20, 1830) * mm, "end": v(-2630, 1830) * mm});
            skLineSegment(sketch, "E23.left", {"start": v(-20, 1850) * mm, "end": v(-20, 1830) * mm});
            skLineSegment(sketch, "E23.right", {"start": v(-2630, 1850) * mm, "end": v(-2630, 1830) * mm});
            skLineSegment(sketch, "E24.bottom", {"start": v(-1325, 1850) * mm, "end": v(-1345, 1850) * mm});
            skLineSegment(sketch, "E24.top", {"start": v(-1325, 3070) * mm, "end": v(-1345, 3070) * mm});
            skLineSegment(sketch, "E24.left", {"start": v(-1325, 1850) * mm, "end": v(-1325, 3070) * mm});
            skLineSegment(sketch, "E24.right", {"start": v(-1345, 1850) * mm, "end": v(-1345, 3070) * mm});
            skSolve(sketch);
        }
        {
            var Q0;
            Q0=qCreatedBy(id+"F8.planeOp",FACE);
            var sketch = newSketch(context, id + "F19", { "sketchPlane" : qUnion([Q0])});
            skLineSegment(sketch, "E25.bottom", {"start": v(-20, 1650) * mm, "end": v(-2630, 1650) * mm});
            skLineSegment(sketch, "E25.top", {"start": v(-20, 1630) * mm, "end": v(-2630, 1630) * mm});
            skLineSegment(sketch, "E25.left", {"start": v(-20, 1650) * mm, "end": v(-20, 1630) * mm});
            skLineSegment(sketch, "E25.right", {"start": v(-2630, 1650) * mm, "end": v(-2630, 1630) * mm});
            skLineSegment(sketch, "E26.0.1.0", {"start": v(-20, 2020) * mm, "end": v(-2630, 2020) * mm});
            skLineSegment(sketch, "E26.0.1.1", {"start": v(-20, 2000) * mm, "end": v(-2630, 2000) * mm});
            skLineSegment(sketch, "E26.0.1.2", {"start": v(-2630, 2020) * mm, "end": v(-2630, 2000) * mm});
            skLineSegment(sketch, "E26.0.1.3", {"start": v(-20, 2020) * mm, "end": v(-20, 2000) * mm});
            skLineSegment(sketch, "E26.0.2.0", {"start": v(-20, 2390) * mm, "end": v(-2630, 2390) * mm});
            skLineSegment(sketch, "E26.0.2.1", {"start": v(-20, 2370) * mm, "end": v(-2630, 2370) * mm});
            skLineSegment(sketch, "E26.0.2.2", {"start": v(-2630, 2390) * mm, "end": v(-2630, 2370) * mm});
            skLineSegment(sketch, "E26.0.2.3", {"start": v(-20, 2390) * mm, "end": v(-20, 2370) * mm});
            skLineSegment(sketch, "E26.0.3.0", {"start": v(-20, 2760) * mm, "end": v(-2630, 2760) * mm});
            skLineSegment(sketch, "E26.0.3.1", {"start": v(-20, 2740) * mm, "end": v(-2630, 2740) * mm});
            skLineSegment(sketch, "E26.0.3.2", {"start": v(-2630, 2760) * mm, "end": v(-2630, 2740) * mm});
            skLineSegment(sketch, "E26.0.3.3", {"start": v(-20, 2760) * mm, "end": v(-20, 2740) * mm});
            skLineSegment(sketch, "E26.direction1", {"start": v(-2630, 1650) * mm, "end": v(-2605, 1650) * mm, "construction": true});
            skLineSegment(sketch, "E26.direction2", {"start": v(-2630, 1650) * mm, "end": v(-2630, 1750) * mm, "construction": true});
            skLineSegment(sketch, "E27.bottom", {"start": v(-725, 848.9) * mm, "end": v(-745, 848.9) * mm});
            skLineSegment(sketch, "E27.top", {"start": v(-725, 140) * mm, "end": v(-745, 140) * mm});
            skLineSegment(sketch, "E27.left", {"start": v(-725, 848.9) * mm, "end": v(-725, 140) * mm});
            skLineSegment(sketch, "E27.right", {"start": v(-745, 848.9) * mm, "end": v(-745, 140) * mm});
            skLineSegment(sketch, "E28.bottom", {"start": v(-1945, 850) * mm, "end": v(-1925, 850) * mm});
            skLineSegment(sketch, "E28.top", {"start": v(-1945, 140) * mm, "end": v(-1925, 140) * mm});
            skLineSegment(sketch, "E28.left", {"start": v(-1945, 850) * mm, "end": v(-1945, 140) * mm});
            skLineSegment(sketch, "E28.right", {"start": v(-1925, 850) * mm, "end": v(-1925, 140) * mm});
            skLineSegment(sketch, "E29.bottom", {"start": v(-1325, 848.9) * mm, "end": v(-1345, 848.9) * mm});
            skLineSegment(sketch, "E29.top", {"start": v(-1325, 140) * mm, "end": v(-1345, 140) * mm});
            skLineSegment(sketch, "E29.left", {"start": v(-1325, 848.9) * mm, "end": v(-1325, 140) * mm});
            skLineSegment(sketch, "E29.right", {"start": v(-1345, 848.9) * mm, "end": v(-1345, 140) * mm});
            skLineSegment(sketch, "E30.bottom", {"start": v(-745, 451) * mm, "end": v(-1925, 451) * mm});
            skLineSegment(sketch, "E30.top", {"start": v(-745, 431) * mm, "end": v(-1925, 431) * mm});
            skLineSegment(sketch, "E30.left", {"start": v(-745, 451) * mm, "end": v(-745, 431) * mm});
            skLineSegment(sketch, "E30.right", {"start": v(-1925, 451) * mm, "end": v(-1925, 431) * mm});
            skSolve(sketch);
        }
        {
            var Q0;
            Q0 = qSketchRegion(id + "F19", true);
            var Q1;
            Q1=qCreatedBy(id+"F11.planeOp",FACE);
            extrude(context, id + "F20", {"entities" : qUnion([Q0]), "operationType" : NewBodyOperationType.ADD, "endBound" : BoundingType.UP_TO_SURFACE, "oppositeDirection" : true, "endBoundEntityFace" : qUnion([Q1]), "depth" : 25 * mm});
        }
        {
            var Q0;
            {var subQ1=sQuery(id+"F0.wireOp",EDGE,"E0.right");var subQ6=makeQuery(id+"F2.opExtrude","CAP_EDGE",EDGE,{"disambiguationData":[OSD([subQ1])],"isStart":false});Q0=makeQuery(id+"F9.imprint","IMPRINT",FACE,{"disambiguationData":[TD([[makeQuery(id+"F9.imprint","IMPRINT",EDGE,{"derivedFrom":subQ6}),-1.0]])]});}
            var sketch = newSketch(context, id + "F21", { "sketchPlane" : qUnion([Q0])});
            skLineSegment(sketch, "E31.bottom", {"start": v(740, 3070) * mm, "end": v(1930, 3070) * mm});
            skLineSegment(sketch, "E31.top", {"start": v(740, 1030) * mm, "end": v(1930, 1030) * mm});
            skLineSegment(sketch, "E31.left", {"start": v(740, 3070) * mm, "end": v(740, 1030) * mm});
            skLineSegment(sketch, "E31.right", {"start": v(1930, 3070) * mm, "end": v(1930, 1030) * mm});
            skLineSegment(sketch, "E32.bottom", {"start": v(2650, 3067) * mm, "end": v(1940, 3067) * mm});
            skLineSegment(sketch, "E32.top", {"start": v(1940, 1033) * mm, "end": v(2650, 1033) * mm});
            skLineSegment(sketch, "E32.left", {"start": v(2650, 3067) * mm, "end": v(2650, 1033) * mm});
            skLineSegment(sketch, "E32.right", {"start": v(1940, 3067) * mm, "end": v(1940, 1033) * mm});
            skPoint(sketch, "E33.oppositeSnap0", {"position": v(2295, 1033) * mm});
            skLineSegment(sketch, "E33.bottom", {"start": v(730, 3067) * mm, "end": v(0, 3067) * mm});
            skLineSegment(sketch, "E33.top", {"start": v(730, 1033) * mm, "end": v(0, 1033) * mm});
            skLineSegment(sketch, "E33.left", {"start": v(730, 3067) * mm, "end": v(730, 1033) * mm});
            skLineSegment(sketch, "E33.right", {"start": v(0, 3067) * mm, "end": v(0, 1033) * mm});
            skLineSegment(sketch, "E34.bottom", {"start": v(1940, 847) * mm, "end": v(2650, 847) * mm});
            skLineSegment(sketch, "E34.top", {"start": v(1940, 143) * mm, "end": v(2650, 143) * mm});
            skLineSegment(sketch, "E34.left", {"start": v(1940, 847) * mm, "end": v(1940, 143) * mm});
            skLineSegment(sketch, "E34.right", {"start": v(2650, 847) * mm, "end": v(2650, 143) * mm});
            skLineSegment(sketch, "E35.bottom", {"start": v(0, 847) * mm, "end": v(730, 847) * mm});
            skLineSegment(sketch, "E35.top", {"start": v(0, 143) * mm, "end": v(730, 143) * mm});
            skLineSegment(sketch, "E35.left", {"start": v(0, 847) * mm, "end": v(0, 143) * mm});
            skLineSegment(sketch, "E35.right", {"start": v(730, 847) * mm, "end": v(730, 143) * mm});
            skLineSegment(sketch, "E36.bottom", {"start": v(1930, 143) * mm, "end": v(1340, 143) * mm});
            skLineSegment(sketch, "E36.top", {"start": v(1930, 847) * mm, "end": v(1340, 847) * mm});
            skLineSegment(sketch, "E36.left", {"start": v(1930, 143) * mm, "end": v(1930, 847) * mm});
            skLineSegment(sketch, "E36.right", {"start": v(1340, 143) * mm, "end": v(1340, 847) * mm});
            skSolve(sketch);
        }
        {
            var Q0;
            Q0 = qSketchRegion(id + "F21", true);
            extrude(context, id + "F22", {"entities" : qUnion([Q0]), "operationType" : NewBodyOperationType.ADD, "oppositeDirection" : true, "depth" : 18 * mm});
        }
    });
